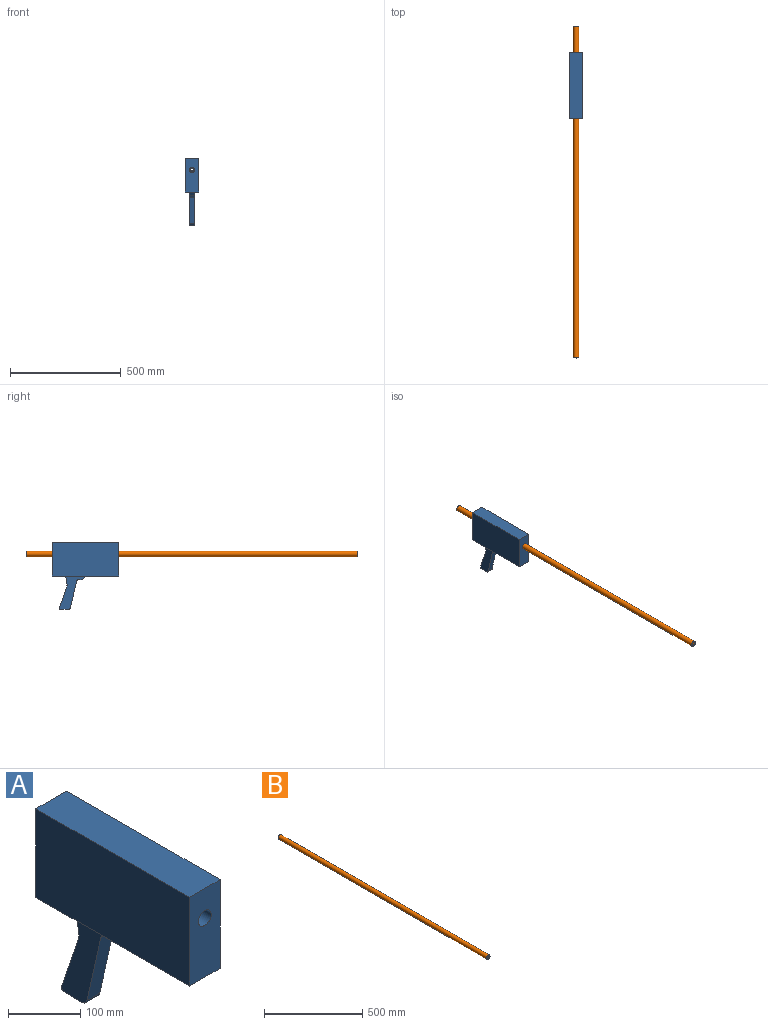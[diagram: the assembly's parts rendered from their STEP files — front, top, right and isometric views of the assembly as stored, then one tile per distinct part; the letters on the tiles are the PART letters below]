
ASSEMBLY  parts=2 mates=1
PART A: 20 faces, bbox 60x300x300 mm
  f0: plane 300x60mm, normal (0,0,-1), area 15505.2mm2, adj f2,f4,f5,f6,f14,f15,f16,f17
  f1: plane 300x60mm, normal (0,0,1), area 18000mm2, adj f2,f4,f5,f6
  f2: plane 300x150mm, normal (-1,0,0), area 45000mm2, adj f0,f1,f5,f6
  f3: cylinder r=12.5mm len=300mm, axis (0,1,0), area 23561.9mm2, adj f5,f6
  f4: plane 300x150mm, normal (1,0,0), area 45000mm2, adj f0,f1,f5,f6
  f5: plane 150x60mm, normal (0,-1,0), area 8509.1mm2, adj f0,f1,f2,f3,f4
  f6: plane 150x60mm, normal (0,1,0), area 8509.1mm2, adj f0,f1,f2,f3,f4
  f7: plane 119.49x26.95mm, normal (0,-0.98,-0.22), area 3062.2mm2, adj f8,f15,f16,f19
  f8: cylinder r=10mm len=25mm, axis (-1,0,0), area 337.2mm2, adj f7,f9,f15,f16
  f9: plane 35.03x25mm, normal (0,0,-1), area 875.8mm2, adj f8,f10,f15,f16
  f10: cylinder r=5mm len=25mm, axis (-1,0,0), area 237.1mm2, adj f9,f11,f15,f16
  f11: plane 98.22x33.24mm, normal (0,0.95,0.32), area 2592.4mm2, adj f10,f12,f15,f16
  f12: cylinder r=15mm len=25mm, axis (-1,0,0), area 183.2mm2, adj f11,f13,f15,f16
  f13: plane 27.88x25mm, normal (0,0.99,-0.16), area 706.3mm2, adj f12,f14,f15,f16
  f14: cylinder r=12mm len=25mm, axis (-1,0,0), area 422.6mm2, adj f0,f13,f15,f16
  f15: plane 150x117.49mm, normal (1,0,0), area 7201.2mm2, adj f0,f7,f8,f9,f10,f11,f12,f13
  f16: plane 150x117.49mm, normal (-1,0,0), area 7201.2mm2, adj f0,f7,f8,f9,f10,f11,f12,f13
  f17: plane 25x17.76mm, normal (0,-0.76,-0.65), area 586.8mm2, adj f0,f15,f16,f18
  f18: plane 25x19.21mm, normal (0,0,-1), area 480.3mm2, adj f15,f16,f17,f19
  f19: cylinder r=6.35mm len=25mm, axis (-1,0,0), area 214.1mm2, adj f7,f15,f16,f18
PART B: 4 faces, bbox 25x1500x25 mm
  f0: cylinder r=6.35mm len=1500mm, axis (0,1,0), area 59847.3mm2, adj f2,f3
  f1: cylinder r=12.5mm len=1500mm, axis (0,1,0), area 117809.7mm2, adj f2,f3
  f2: plane 25x25mm, normal (0,-1,0), area 364.2mm2, adj f0,f1
  f3: plane 25x25mm, normal (0,1,0), area 364.2mm2, adj f0,f1
PLACE A t=(0,750,0)mm fixed
PLACE B t=(0,118.81,0)mm
MATE slider A.f3 <-> B.f1  axis (0,1,0) through (0,750,0)mm
